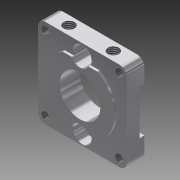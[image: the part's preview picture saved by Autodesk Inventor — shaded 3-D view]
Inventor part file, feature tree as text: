
AUTODESK INVENTOR PART (.ipt)
format: ipt  version: 2014 SP1 (Build 180222100, 222)  size: 247,296 bytes
history: native  units: in
note: dims shown in document units (in); Inventor stores cm internally (conversion verified against a paired STEP export)
features: thread x8, extrude x7, sketch x5, fillet x2
ambient origin geometry x8: Origin, YZ Plane, XZ Plane, XY Plane, X Axis, Y Axis, Z Axis, Center Point
bodies: Solid1 (feature_tree)
feature tree (22):
  extrude  "Extrusion1"  Depth=1.5in
  fillet  "Fillet1"  Radius=0.1378in
  extrude  "Extrusion2"  Depth=0.125in
  extrude  "Extrusion3"  Depth=0.125in
  thread  "Thread1"  [1 undecoded]
  thread  "Thread2"  [1 undecoded]
  thread  "Thread3"  [1 undecoded]
  thread  "Thread4"  [1 undecoded]
  thread  "Thread5"  [1 undecoded]
  thread  "Thread6"  [1 undecoded]
  thread  "Thread7"  [1 undecoded]
  thread  "Thread8"  [1 undecoded]
  extrude  "Extrusion4"  Depth=0.375in
  fillet  "Fillet2"  Radius=0.375in
  sketch  "Sketch5"  dims[d32=0.185in d33=0.185in d34=0.3in d35=0.0in d36=0.15in d37=0.375in d38=0.375in d39=0.185in d40=0.185in d41=0.3in d42=0.0in d43=1.0in d44=0.0in d45=1.0in d46=0.0in d47=1.0in d48=0.0in d49=1.0in d50=0.0in d51=1.0in d52=0.0in d53=1.0in d54=0.0in d55=1.0in d56=0.0in d57=1.0in d58=0.0in d59=0.748in d60=0.0197in d61=0.6in d62=0.0787in d63=0.0in d64=0.125in d65=1.1614in d66=1.1417in d67=0.315in d68=0.5906in d69=0.5807in d70=0.0394in d71=0.0in d72=0.185in d73=0.3in d74=0.0in d75=0.2213in d76=0.0in]
  extrude  "Extrusion5"  Depth=0.2213in
  extrude  "Extrusion6"  Depth=0.3in TaperAngle=0.0deg
  extrude  "Extrusion7"  Depth=0.2213in
  sketch  "Sketch1"  dims[d0=1.5in d1=1.5in d2=0.1378in]
  sketch  "Sketch2"  dims[d3=0.7874in d5=1.25in d6=0.7874in d8=1.25in d11=0.125in]
  sketch  "Sketch3"  dims[d12=0.125in d13=0.75in d14=0.689in d15=0.5in d16=0.125in d17=0.125in d18=0.075in d22=1.5748in d24=360.0deg d26=0.3in d27=0.0in d28=0.125in]
  sketch  "Sketch4"  dims[d29=0.15in d30=0.375in d31=0.375in]
note: 8 required parameter values undecoded (feature->parameter linkage not recoverable at this tier; creation-order binding heuristic only, values carry confidence <= 0.55)
